# Revit family: 1RA-IN_Double Angle_Left_DN10-15_RFA
name_source: partatom
category: Pipe Accessories
units: mm (PartAtom-declared; Revit-internal decimal feet)

## family parameters
Always vertical = Yes
Cut with Voids When Loaded = No
OmniClass Number = 23.65.55.14.17
OmniClass Title = Adjusting/Controlling Valves for Liquid Services
Part Type = Valve - Breaks Into
Round Connector Dimension = Use Diameter
Shared = No
Work Plane-Based = No

## types (2) — shared parameters
Connection = Internal thread
Description = Thermostatic Radiator Valve
H1 = 15 mm  [stored 0.0492126 ft]
HH = 22 mm  [stored 0.0721785 ft]
HT = 48 mm  [stored 0.15748 ft]
IfcExportAs = IfcValveType
IfcExportType = RA-IN
LOD 200 = No
LOD 350 = Yes
Manufacturer = Danfoss
Max Differential Pressure = 0.6 bar
Max Medium Temperature = 120 ˚C
Max Operating Pressure = 10 bar
RB1 = 11.3 mm  [stored 0.0370735 ft]
RB3 = 12.8 mm  [stored 0.0419948 ft]
RV6 = 10 mm  [stored 0.0328084 ft]
SH = 33 mm  [stored 0.108268 ft]
Setting Range = 1-4,N
URL = https://store.danfoss.com
Valve Body Material = Danfoss Brass (Nickel plated)

## per-type parameters (varying)
- RA-IN_Double Angle_Left_DN10_013G6572: D=10 mm  [stored 0.0328084 ft]; DB4=25.6 mm  [stored 0.0839895 ft]; H=63.5 mm  [stored 0.208333 ft]; Kvs=0.7 m³/h; L=64.8 mm  [stored 0.212598 ft]; L1=16 mm  [stored 0.0524934 ft]; L2=6 mm  [stored 0.019685 ft]; L3=3 mm  [stored 0.00984252 ft]; L4=8.5 mm  [stored 0.0278871 ft]; L5=27 mm  [stored 0.0885827 ft]; L6=16 mm  [stored 0.0524934 ft]; LL=52 mm; L_nut thread1=22 mm  [stored 0.0721785 ft]; L_nut thread2=27 mm  [stored 0.0885827 ft]; Model=013G6572; Model Type=RA-IN_Double Angle_Left_DN10; RB=12.8 mm  [stored 0.0419948 ft]; RB2=10.5 mm  [stored 0.0344488 ft]; RB3_1=10.3 mm; RV1=10.5 mm  [stored 0.0344488 ft]; RV1_1=9.8 mm  [stored 0.0321522 ft]; RV2=9.8 mm  [stored 0.0321522 ft]; RV3=13.5 mm  [stored 0.0442913 ft]; RV4=8.5 mm  [stored 0.0278871 ft]; R_200=12.6 mm  [stored 0.0413386 ft]; R_200_1=15.5 mm  [stored 0.050853 ft]; SL=33.5 mm  [stored 0.109908 ft]; W=40.5 mm; Weight=0.23 kg
- RA-IN_Double Angle_Left_DN15_013G6574: D=15 mm  [stored 0.0492126 ft]; DB4=25 mm  [stored 0.082021 ft]; H=65.32 mm; Kvs=0.9 m³/h; L=73.59 mm  [stored 0.241437 ft]; L1=17 mm; L2=4 mm  [stored 0.0131234 ft]; L3=6 mm  [stored 0.019685 ft]; L4=10 mm  [stored 0.0328084 ft]; L5=33 mm  [stored 0.108268 ft]; L6=17 mm; LL=58 mm  [stored 0.190289 ft]; L_nut thread1=27 mm  [stored 0.0885827 ft]; L_nut thread2=30 mm  [stored 0.0984252 ft]; Model=013G6574; Model Type=RA-IN_Double Angle_Left_DN15; RB=15.59 mm  [stored 0.0511483 ft]; RB2=13 mm; RB3_1=1 mm  [stored 0.00328084 ft]; RV1=13 mm; RV1_1=11.5 mm  [stored 0.0377297 ft]; RV2=11.5 mm  [stored 0.0377297 ft]; RV3=15 mm  [stored 0.0492126 ft]; RV4=10.5 mm  [stored 0.0344488 ft]; R_200=15.59 mm  [stored 0.0511483 ft]; R_200_1=17.32 mm; SL=37 mm  [stored 0.121391 ft]; W=48 mm  [stored 0.15748 ft]; Weight=0.29 kg

note: [stored X ft] marks values corroborated as IEEE doubles in the binary element streams (Revit-internal decimal feet)

## geometry (parser evidence)
native form markers: Sweep x5
no freeform markers — native parametric forms only
